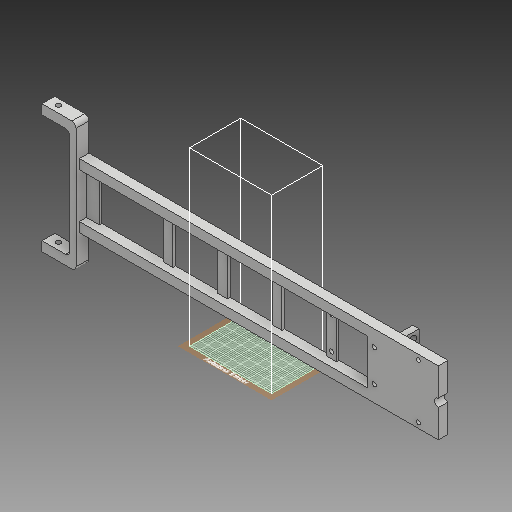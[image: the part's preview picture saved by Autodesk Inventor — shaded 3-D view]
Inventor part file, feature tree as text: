
AUTODESK INVENTOR PART (.ipt)
format: ipt  version: 2018 (Build 220112000, 112)  size: 894,976 bytes
history: native  units: mm
features: sketch x61, extrude x49, fillet x11, hole x6
ambient origin geometry x8: Origin, YZ Plane, XZ Plane, XY Plane, X Axis, Y Axis, Z Axis, Center Point
bodies: Solid1 (feature_tree)
feature tree (127):
  extrude  "Extrusion1"  Depth=50.0mm
  hole  "Hole1"  [1 undecoded]
  hole  "Hole2"  [1 undecoded]
  extrude  "Extrusion2"  Depth=25.0mm
  extrude  "Extrusion3"  Depth=25.0mm
  extrude  "Extrusion4"  Depth=5.0mm
  sketch  "Sketch7"  dims[d25=10.0mm d26=5.0mm]
  extrude  "Extrusion5"  Depth=5.0mm
  extrude  "Extrusion6"  Depth=35.0mm
  extrude  "Extrusion7"  Depth=35.0mm
  extrude  "Extrusion8"  Depth=35.0mm
  extrude  "Extrusion9"  Depth=2.0mm TaperAngle=0.0deg
  extrude  "Extrusion10"  Depth=7.5mm TaperAngle=0.0deg
  extrude  "Extrusion11"  Depth=10.0mm
  extrude  "Extrusion12"  Depth=7.5mm
  fillet  "Fillet1"  Radius=7.5mm
  fillet  "Fillet2"  Radius=25.0mm
  fillet  "Fillet3"  Radius=3.0mm
  fillet  "Fillet4"  Radius=3.2mm
  fillet  "Fillet5"  Radius=2.1mm
  fillet  "Fillet6"  Radius=5.5mm
  extrude  "Extrusion13"  Depth=92.5mm TaperAngle=0.0deg
  sketch  "Sketch17"  dims[d58=4.25mm d59=241.0mm d60=0.0mm]
  hole  "Hole3"  [1 undecoded]
  hole  "Hole4"  [1 undecoded]
  extrude  "Extrusion14"  Depth=5.0mm
  extrude  "Extrusion15"  Depth=2.5mm TaperAngle=0.0deg
  extrude  "Extrusion16"  Depth=6.35mm
  extrude  "Extrusion17"  Depth=2.5mm
  extrude  "Extrusion18"  Depth=14.55mm TaperAngle=0.0deg
  extrude  "Extrusion19"  Depth=0.1mm
  extrude  "Extrusion20"  Depth=3.25mm
  extrude  "Extrusion21"  Depth=3.25mm
  hole  "Hole5"  [1 undecoded]
  extrude  "Extrusion22"  Depth=2.0mm
  extrude  "Extrusion23"  Depth=15.0mm
  extrude  "Extrusion24"  Depth=10.0mm TaperAngle=0.0deg
  hole  "Hole6"  [1 undecoded]
  extrude  "Extrusion25"  Depth=100.0mm TaperAngle=0.0deg
  extrude  "Extrusion26"  Depth=2.0mm TaperAngle=0.0deg
  sketch  "Sketch35"  dims[d116=3.3mm d117=3.3mm]
  extrude  "Extrusion29"  Depth=3.3mm
  extrude  "Extrusion30"  Depth=3.3mm
  extrude  "Extrusion31"  Depth=5.5mm TaperAngle=0.0deg
  extrude  "Extrusion32"  Depth=8.0mm
  sketch  "Sketch43"  dims[d136=15.825mm d137=3.5mm]
  fillet  "Fillet8"  Radius=17.0mm
  extrude  "Extrusion33"  Depth=8.5mm
  extrude  "Extrusion34"  Depth=3.5mm
  extrude  "Extrusion35"  Depth=3.3mm
  extrude  "Extrusion36"  Depth=3.3mm
  extrude  "Extrusion37"  Depth=7.5mm TaperAngle=0.0deg
  fillet  "Fillet9"  Radius=100.0mm
  fillet  "Fillet10"  Radius=3.75mm
  fillet  "Fillet11"  Radius=100.0mm
  fillet  "Fillet12"  Radius=100.0mm
  sketch  "Sketch49"  dims[d172=10.0mm d173=0.0mm d174=74.724mm]
  extrude  "Extrusion38"  Depth=5.5mm TaperAngle=0.0deg
  extrude  "Extrusion39"  Depth=10.0mm
  extrude  "Extrusion40"  Depth=85.515mm
  extrude  "Extrusion41"  Depth=5.0mm
  extrude  "Extrusion42"  Depth=5.0mm
  extrude  "Extrusion43"  Depth=5.0mm
  sketch  "Sketch58"  dims[d189=2.0mm d190=1.0mm d191=0.0mm]
  extrude  "Extrusion45"  Depth=2.0mm TaperAngle=0.0deg
  extrude  "Extrusion46"  Depth=2.0mm TaperAngle=0.0deg
  extrude  "Extrusion47"  Depth=1.0mm TaperAngle=0.0deg
  extrude  "Extrusion48"  Depth=10.0mm
  extrude  "Extrusion49"  Depth=20.0mm
  extrude  "Extrusion50"  Depth=7.5mm
  extrude  "Extrusion51"  Depth=2.5mm TaperAngle=0.0deg
  extrude  "Extrusion52"  Depth=3.25mm
  sketch  "Sketch1"  dims[d0=50.0mm d1=50.0mm]
  sketch  "Sketch2"  dims[d2=240.0mm d3=7.5mm]
  sketch  "Sketch3"  dims[d4=7.5mm d5=7.5mm d6=0.0mm]
  sketch  "Sketch4"  dims[d7=6.35mm d8=6.0mm d9=4.0mm d10=2.0mm d11=90.0deg d12=8.0mm d13=20.594885mm d14=25.0mm]
  sketch  "Sketch5"  dims[d15=3.3mm d16=6.0mm d17=4.0mm d18=2.0mm d19=90.0deg d20=8.0mm d21=20.594885mm d22=25.0mm]
  sketch  "Sketch6"  dims[d23=180.0deg d24=5.0mm]
  sketch  "Sketch8"  dims[d27=17.5mm d28=0.0mm d30=35.0mm]
  sketch  "Sketch9"  dims[d31=35.0mm d32=35.0mm]
  sketch  "Sketch10"  dims[d33=35.0mm d34=35.0mm]
  sketch  "Sketch11"  dims[d35=35.0mm d36=2.0mm d37=0.0mm]
  sketch  "Sketch12"  dims[d38=10.0mm d39=7.5mm d40=0.0mm]
  sketch  "Sketch13"  dims[d41=100.0mm d42=10.0mm]
  sketch  "Sketch14"  dims[d43=7.5mm d44=0.0mm d45=7.5mm d46=7.5mm d47=25.0mm d48=0.0mm d49=3.0mm d50=3.2mm d51=2.1mm d52=5.5mm]
  sketch  "Sketch15"  dims[d53=3.3mm d54=92.5mm d55=0.0mm]
  sketch  "Sketch16"  dims[d56=5.5mm d57=3.3mm]
  sketch  "Sketch18"  dims[d61=4.44mm d62=5.0mm]
  sketch  "Sketch19"  dims[d63=2.5mm d64=91.25mm d65=0.0mm]
  sketch  "Sketch20"  dims[d66=30.0mm d67=6.35mm]
  sketch  "Sketch21"  dims[d68=3.8mm d69=0.0mm d70=2.5mm]
  sketch  "Sketch22"  dims[d71=14.55mm d72=0.0mm d73=14.55mm d74=0.0mm]
  sketch  "Sketch23"  dims[d75=0.1mm d76=0.1mm]
  sketch  "Sketch24"  dims[d77=3.25mm d78=3.25mm]
  sketch  "Sketch25"  dims[d79=3.25mm d80=3.25mm]
  sketch  "Sketch26"  dims[d81=35.0mm d82=10.0mm]
  sketch  "Sketch27"  dims[d83=2.0mm d84=0.0mm d85=3.6mm]
  sketch  "Sketch28"  dims[d86=3.6mm]
  sketch  "Sketch29"  dims[d87=3.3mm d88=6.0mm d89=4.0mm d90=2.0mm d91=90.0deg d92=15.0mm d93=20.594885mm]
  sketch  "Sketch30"  dims[d94=3.3mm d95=6.0mm d96=4.0mm d97=2.0mm d98=90.0deg d99=15.0mm d100=20.594885mm d101=6.0mm]
  sketch  "Sketch31"  dims[d102=20.0mm d103=0.0mm d104=10.0mm d105=0.0mm]
  sketch  "Sketch32"  dims[d106=2.0mm d107=0.0mm d108=4.0mm]
  sketch  "Sketch33"  dims[d109=100.0mm d110=0.0mm d111=100.0mm d112=0.0mm]
  sketch  "Sketch34"  dims[d113=5.0mm d114=2.0mm d115=0.0mm]
  sketch  "Sketch39"  dims[d118=3.3mm d119=3.3mm]
  sketch  "Sketch40"  dims[d120=2.0mm d121=0.0mm d122=5.5mm d123=0.0mm]
  sketch  "Sketch41"  dims[d124=3.3mm d125=6.0mm d126=4.0mm d127=2.0mm d128=90.0deg d129=8.0mm d130=20.594885mm d131=42.0mm d132=17.0mm]
  sketch  "Sketch42"  dims[d133=21.0mm d135=8.5mm]
  sketch  "Sketch44"  dims[d138=21.0mm d139=3.3mm]
  sketch  "Sketch45"  dims[d140=3.3mm d141=3.3mm]
  sketch  "Sketch46"  dims[d142=10.0mm d143=0.0mm d144=7.5mm d145=0.0mm d146=100.0mm d147=0.0mm]
  sketch  "Sketch47"  dims[d148=5.0mm d149=6.0mm d150=4.0mm d151=2.0mm d152=90.0deg d153=15.0mm d154=0.0mm d155=3.75mm d156=100.0mm d157=0.0mm d158=100.0mm d159=0.0mm]
  sketch  "Sketch48"  dims[d169=3.0mm d170=5.5mm d171=0.0mm]
  sketch  "Sketch50"  dims[d175=74.724mm d176=85.515mm]
  sketch  "Sketch51"  dims[d177=5.0mm d178=85.515mm]
  sketch  "Sketch52"  dims[d179=5.0mm d180=85.515mm]
  sketch  "Sketch53"  dims[d181=5.0mm d182=85.515mm]
  sketch  "Sketch54"  dims[d183=5.0mm d184=2.0mm d185=0.0mm]
  sketch  "Sketch56"  dims[d186=10.0mm d187=2.0mm d188=0.0mm]
  sketch  "Sketch59"  dims[d192=2.0mm d193=0.0mm d194=10.0mm]
  sketch  "Sketch60"  dims[d195=1.0mm d196=0.0mm d197=20.0mm]
  sketch  "Sketch62"  dims[d198=1.0mm d199=0.0mm d200=7.5mm]
  sketch  "Sketch63"  dims[d201=5.0mm d202=2.5mm d203=0.0mm]
  sketch  "Sketch64"  dims[d204=3.25mm d205=3.25mm]
  sketch  "Sketch65"  dims[d206=3.25mm]
  sketch  "Sketch66"  dims[d207=3.25mm]
  sketch  "Sketch67"  dims[d208=6.25mm d209=9.58mm d210=250.0mm d211=0.0mm d212=5.25mm d213=4.3mm d214=0.0mm d215=4.3mm d216=0.0mm d218=9.7mm d219=100.0mm d220=0.0mm d221=9.8mm d222=4.5mm d223=4.3mm d224=0.0mm d225=9.8mm d226=4.3mm d227=0.0mm d230=20.0mm d231=10.0mm d232=0.0mm d233=5.0mm d234=5.0mm d235=10.0mm d236=0.0mm d237=3.65mm d238=7.5mm d239=0.0mm d240=7.5mm d241=0.0mm d242=50.0mm d243=0.0mm d244=20.0mm d245=1.0mm d246=7.5mm d247=0.0mm d248=7.5mm d249=0.0mm d250=1.0mm d251=0.0mm]
note: 6 required parameter values undecoded (feature->parameter linkage not recoverable at this tier; creation-order binding heuristic only, values carry confidence <= 0.55)
